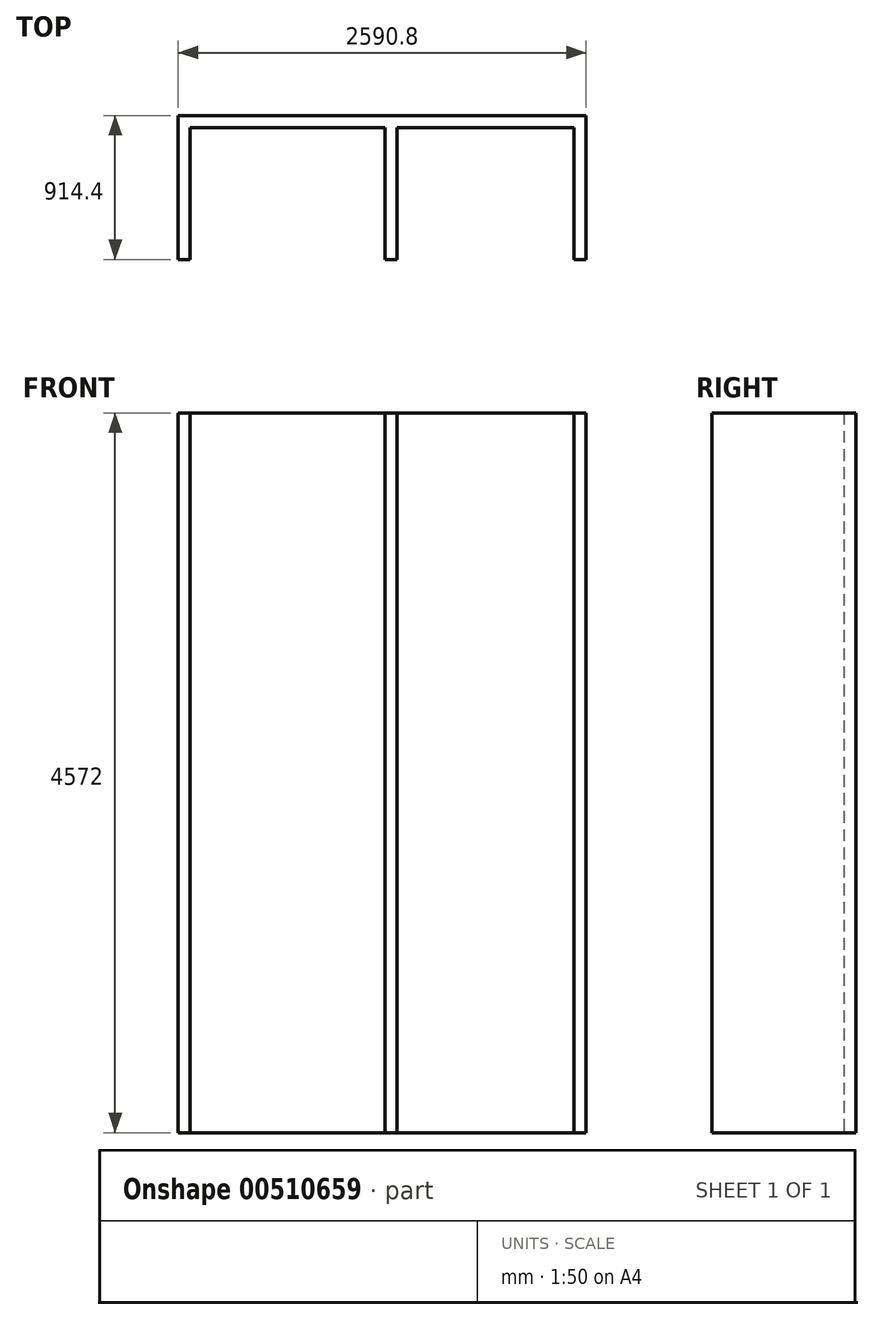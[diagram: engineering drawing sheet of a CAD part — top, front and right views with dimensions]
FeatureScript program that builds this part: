
annotation { "Feature Type Name" : "Feature", "Feature Type Description" : "" }
export const myFeature = defineFeature(function(context is Context, id is Id, definition is map)
    precondition{}
    {
        {
            var Q0;
            Q0=qCreatedBy(makeId("Top.planeOp"),FACE);
            var sketch = newSketch(context, id + "F0", { "sketchPlane" : qUnion([Q0])});
            skLineSegment(sketch, "E0", {"start": v(-1277.41, -410.42) * mm, "end": v(-1277.41, 503.98) * mm});
            skLineSegment(sketch, "E1", {"start": v(-1277.41, 503.98) * mm, "end": v(1313.39, 503.98) * mm});
            skLineSegment(sketch, "E2", {"start": v(1313.39, 503.98) * mm, "end": v(1313.39, -410.42) * mm});
            skLineSegment(sketch, "E3", {"start": v(1313.39, -410.42) * mm, "end": v(1237.19, -410.42) * mm});
            skLineSegment(sketch, "E4", {"start": v(1237.19, -410.42) * mm, "end": v(1237.19, 427.78) * mm});
            skLineSegment(sketch, "E5", {"start": v(1237.19, 427.78) * mm, "end": v(112.37, 427.78) * mm});
            skLineSegment(sketch, "E6", {"start": v(112.37, 427.78) * mm, "end": v(112.37, -410.42) * mm});
            skLineSegment(sketch, "E7", {"start": v(112.37, -410.42) * mm, "end": v(36.17, -410.42) * mm});
            skLineSegment(sketch, "E8", {"start": v(36.17, -410.42) * mm, "end": v(36.17, 427.78) * mm});
            skLineSegment(sketch, "E9", {"start": v(36.17, 427.78) * mm, "end": v(-1201.21, 427.78) * mm});
            skLineSegment(sketch, "E10", {"start": v(-1201.21, 427.78) * mm, "end": v(-1201.21, -410.42) * mm});
            skLineSegment(sketch, "E11", {"start": v(-1201.21, -410.42) * mm, "end": v(-1277.41, -410.42) * mm});
            skSolve(sketch);
        }
        {
            var Q0;
            Q0 = qSketchRegion(id + "F0", true);
            extrude(context, id + "F1", {"entities" : qUnion([Q0]), "depth" : 4572 * mm, "offsetDistance" : 30.48 * mm});
        }
    });
